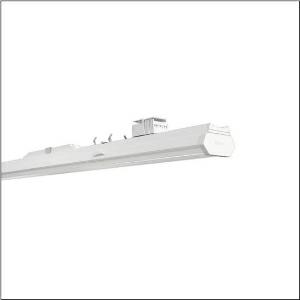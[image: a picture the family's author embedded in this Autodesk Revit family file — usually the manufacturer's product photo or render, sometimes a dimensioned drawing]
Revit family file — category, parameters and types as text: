
# Revit family: licross_r__21_protected_mo_52td12dn4a5g3c_a968
name_source: partatom
category: Lighting Fixtures
units: mm (PartAtom-declared; Revit-internal decimal feet)

## family parameters
Cut with Voids When Loaded = No
Host = Face
Light Source = No
Part Type = Normal
Room Calculation Point = No
Round Connector Dimension = Use Diameter
Shared = No

## types (1)
- --- (1 x LED, 940 lm, 6.8 W, 4000K)
    Apparent Load = 7 VA
    CIE Flux Codes = 73 92 98 99 100
    Color Rendering = 80
    Color Temperature = 4000K
    Default Elevation = 1800 mm
    Description = Licross® 21 Protected MO, luminaire insert, of sheet steel, galvanised, coil coated, white, length: 1.500mm, width: 90mm, height: 103mm, LED rated luminous flux: 10.700lm, light colour: 840, control gear: DALI 2 (for two DALI lines), with plug, 6-pole, with phase selection, for trunking rail, 14-core, mains connection: 220..240V, AC, 50/60Hz, rated input power: 66W, for trunking rail, 14-core, halogen-free wiring, for emergency light function, converter,control gear: single battery element, battery: LiFePO4, 9Ah, primary light control with lens, of plastic, primary optical cover: cover, of PMMA, light emission: direct distribution, primary light characteristic: symmetric, protection rating (complete): IP54, insulation class (complete): insulation class I (protective earthing), certification: CE, UKCA, protection symbol: D if used in an environment with non-conductive dust loads with corresponding accessories, impact resistance: IK06, permissible ambient temperature for indoor applications: +5..+35°C, standard: EN 60598-2-22, LABS conformity tested according to VDMA 24364:2018-05, reducing of maximum allowable ambient temperature of 5°C with ceiling mounting, corresponds to IFS (International Featured Standards) requirements for safety and quality in the food industry, packaging unit: 1 piece
    Height = 92 mm
    Lamp = 1 x LED
    Lamp Light Flux = 940 lm
    Lamp Power = 6.8 W
    Lamp count = 1
    Length = 1500 mm
    Luminous efficacy = 138 lm/W
    Manufacturer = Siteco
    ModVariant = No
    Model = 52TD12DN4A5G3C
    Mounting Place = Ceiling
    Mounting Type = Pendant
    Number of Poles = 1
    OnlyDefault = Yes
    Power Factor = 1
    Product Name = Licross® 21 Protected MO
    Product group = luminaire insert
    ProductGroupID = 902
    Protection Class = Protection class I
    Protection Degree = IP 54
    RLX_Detail_Level = 1
    RLX_Emergency_Light_Flux = 0 lm
    RLX_Emergency_Type = 0
    RLX_Emergency_Type_DB = No
    RlxData = <blob elided: 24821 chars, md5=20a49c9f>
    Socket = socket
    Standby Power = 0 W
    System Light Flux = 940 lm
    System Power = 7 W
    Type Comments = : emergency light operation: 3 h
    Type Image = l_1256148.jpg
    URL = http://relux.com
    VarID = @adj_110932
    Voltage = 0 V
    Weight = 0.00 kg
    Width = 88 mm

## geometry (parser evidence)
native form markers: Blend x4, Sweep x10
no freeform markers — native parametric forms only
